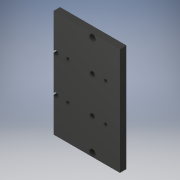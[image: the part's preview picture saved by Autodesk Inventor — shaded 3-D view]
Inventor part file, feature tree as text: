
AUTODESK INVENTOR PART (.ipt)
format: ipt  version: 2017 (Build 210142000, 142)  size: 190,976 bytes
history: native  units: in
note: dims shown in document units (in); Inventor stores cm internally (conversion verified against a paired STEP export)
features: extrude x4, sketch x4
ambient origin geometry x8: Origin, YZ Plane, XZ Plane, XY Plane, X Axis, Y Axis, Z Axis, Center Point
bodies: Solid1 (feature_tree)
feature tree (8):
  extrude  "Extrusion1"  Depth=4.25in
  extrude  "Extrusion2"  Depth=1.5in
  extrude  "Extrusion3"  Depth=1.5in
  extrude  "Extrusion4"  Depth=0.0625in
  sketch  "Sketch1"  dims[d0=2.625in d1=4.25in]
  sketch  "Sketch3"  dims[d2=0.25in d3=0.0in d11=1.5in]
  sketch  "Sketch4"  dims[d12=1.5in d13=0.5in]
  sketch  "Sketch5"  dims[d14=1.45in d15=1.45in d16=0.125in d17=0.125in d18=0.125in d19=0.125in d20=0.125in d21=0.125in d22=0.125in d23=0.125in d24=1.25in d25=0.25in d26=1.25in d27=0.25in d28=0.25in d29=0.0in d30=0.1875in d31=0.1875in d32=0.1875in d33=0.1875in d34=0.125in d35=0.0in d36=0.1875in d37=0.7874in d39=1.5in d40=0.7874in d42=1.5in d45=0.0625in d46=0.0in]
